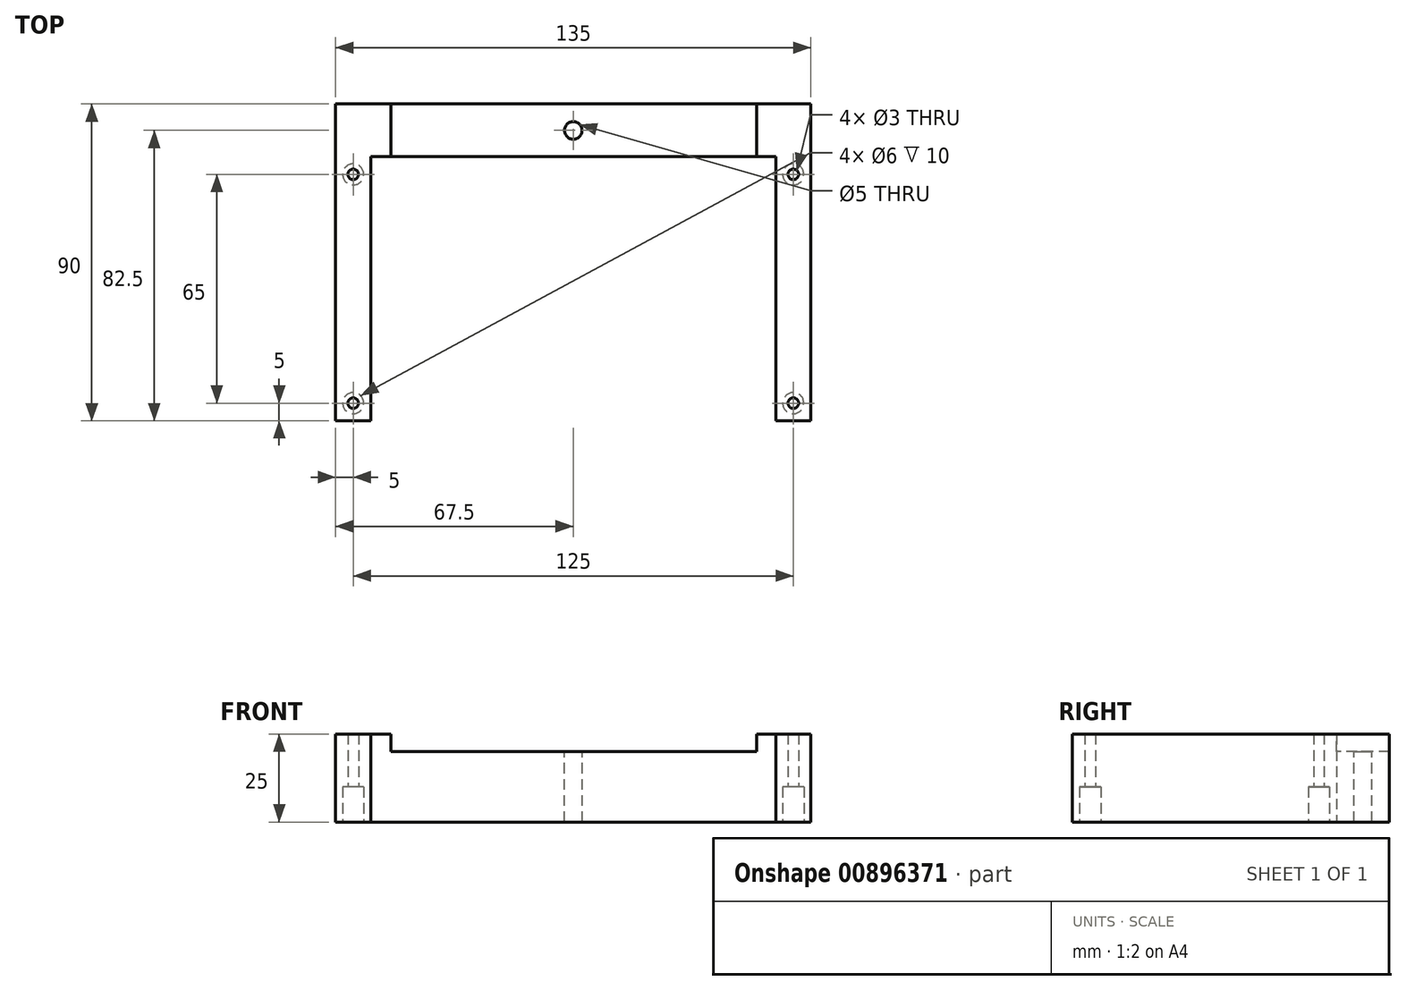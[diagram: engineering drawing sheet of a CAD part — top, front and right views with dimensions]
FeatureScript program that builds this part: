
annotation { "Feature Type Name" : "Feature", "Feature Type Description" : "" }
export const myFeature = defineFeature(function(context is Context, id is Id, definition is map)
    precondition{}
    {
        {
            var Q0;
            Q0=qCreatedBy(makeId("Top.planeOp"),FACE);
            var sketch = newSketch(context, id + "F0", { "sketchPlane" : qUnion([Q0])});
            skCircle(sketch, "E0", {"center": v(-62.5, 65) * mm, "radius": 1.5 * mm});
            skCircle(sketch, "E1", {"center": v(62.5, 65) * mm, "radius": 1.5 * mm});
            skCircle(sketch, "E2", {"center": v(62.5, 0) * mm, "radius": 1.5 * mm});
            skCircle(sketch, "E3", {"center": v(-62.5, 0) * mm, "radius": 1.5 * mm});
            skLineSegment(sketch, "E4", {"start": v(-62.5, 65) * mm, "end": v(62.5, 65) * mm, "construction": true});
            skLineSegment(sketch, "E5", {"start": v(62.5, 0) * mm, "end": v(-62.5, 0) * mm, "construction": true});
            skLineSegment(sketch, "E6", {"start": v(-62.5, 65) * mm, "end": v(-62.5, 0) * mm, "construction": true});
            skLineSegment(sketch, "E7", {"start": v(62.5, 65) * mm, "end": v(62.5, 0) * mm, "construction": true});
            skLineSegment(sketch, "E8.bottom", {"start": v(57.5, 85) * mm, "end": v(67.5, 85) * mm});
            skLineSegment(sketch, "E8.top", {"start": v(57.5, -5) * mm, "end": v(67.5, -5) * mm});
            skLineSegment(sketch, "E8.left", {"start": v(57.5, 85) * mm, "end": v(57.5, -5) * mm});
            skLineSegment(sketch, "E8.right", {"start": v(67.5, 85) * mm, "end": v(67.5, -5) * mm});
            skLineSegment(sketch, "E9.MirrorCS", {"start": v(-57.5, -5) * mm, "end": v(-67.5, -5) * mm});
            skLineSegment(sketch, "E10.MirrorCS", {"start": v(-67.5, 85) * mm, "end": v(-67.5, -5) * mm});
            skLineSegment(sketch, "E11.MirrorCS", {"start": v(-57.5, 85) * mm, "end": v(-57.5, -5) * mm});
            skLineSegment(sketch, "E12.MirrorCS", {"start": v(-57.5, 85) * mm, "end": v(-67.5, 85) * mm});
            skLineSegment(sketch, "E13", {"start": v(62.5, 65) * mm, "end": v(62.5, 80.02) * mm, "construction": true});
            skPoint(sketch, "E14", {"position": v(62.5, 85) * mm});
            skLineSegment(sketch, "E15.bottom", {"start": v(-57.5, 85) * mm, "end": v(57.5, 85) * mm});
            skLineSegment(sketch, "E15.top", {"start": v(-57.5, 70) * mm, "end": v(57.5, 70) * mm});
            skLineSegment(sketch, "E15.left", {"start": v(-57.5, 85) * mm, "end": v(-57.5, 70) * mm});
            skLineSegment(sketch, "E15.right", {"start": v(57.5, 85) * mm, "end": v(57.5, 70) * mm});
            skCircle(sketch, "E16", {"center": v(-62.5, 65) * mm, "radius": 3 * mm});
            skCircle(sketch, "E17", {"center": v(-62.5, 0) * mm, "radius": 3 * mm});
            skCircle(sketch, "E18", {"center": v(62.5, 0) * mm, "radius": 3 * mm});
            skCircle(sketch, "E19", {"center": v(62.5, 65) * mm, "radius": 3 * mm});
            skSolve(sketch);
        }
        {
            var Q0;
            Q0=makeQuery(id+"F0.imprint","IMPRINT",FACE,{"disambiguationData":[TD([[makeQuery(id+"F0.imprint","IMPRINT",EDGE,{"derivedFrom":sQuery(id+"F0.wireOp",EDGE,"E15.bottom")}),-1.0]])]});
            var Q1;
            Q1=makeQuery(id+"F0.imprint","IMPRINT",FACE,{"disambiguationData":[TD([[makeQuery(id+"F0.imprint","IMPRINT",EDGE,{"derivedFrom":sQuery(id+"F0.wireOp",EDGE,"E9.MirrorCS")}),-1.0]])]});
            var Q2;
            Q2=makeQuery(id+"F0.imprint","IMPRINT",FACE,{"disambiguationData":[TD([[makeQuery(id+"F0.imprint","IMPRINT",EDGE,{"derivedFrom":sQuery(id+"F0.wireOp",EDGE,"E8.bottom")}),-1.0]])]});
            var Q3;
            Q3=makeQuery(id+"F0.imprint","IMPRINT",FACE,{"disambiguationData":[TD([[makeQuery(id+"F0.imprint","IMPRINT",EDGE,{"derivedFrom":sQuery(id+"F0.wireOp",EDGE,"E1")}),-1.0]])]});
            var Q4;
            Q4=makeQuery(id+"F0.imprint","IMPRINT",FACE,{"disambiguationData":[TD([[makeQuery(id+"F0.imprint","IMPRINT",EDGE,{"derivedFrom":sQuery(id+"F0.wireOp",EDGE,"E2")}),-1.0]])]});
            var Q5;
            Q5=makeQuery(id+"F0.imprint","IMPRINT",FACE,{"disambiguationData":[TD([[makeQuery(id+"F0.imprint","IMPRINT",EDGE,{"derivedFrom":sQuery(id+"F0.wireOp",EDGE,"E3")}),-1.0]])]});
            var Q6;
            Q6=makeQuery(id+"F0.imprint","IMPRINT",FACE,{"disambiguationData":[TD([[makeQuery(id+"F0.imprint","IMPRINT",EDGE,{"derivedFrom":sQuery(id+"F0.wireOp",EDGE,"E0")}),-1.0]])]});
            extrude(context, id + "F1", {"entities" : qUnion([Q0, Q1, Q2, Q3, Q4, Q5, Q6]), "depth" : 25 * mm, "offsetDistance" : 25 * mm});
        }
        {
            var Q0;
            Q0=makeQuery(id+"F1.opExtrude","CAP_FACE",FACE,{"disambiguationData":[OSD([sQuery(id+"F0.wireOp",EDGE,"E0"),sQuery(id+"F0.wireOp",EDGE,"E1"),sQuery(id+"F0.wireOp",EDGE,"E2"),sQuery(id+"F0.wireOp",EDGE,"E3"),sQuery(id+"F0.wireOp",EDGE,"E8.bottom"),sQuery(id+"F0.wireOp",EDGE,"E8.top"),sQuery(id+"F0.wireOp",EDGE,"E8.left"),sQuery(id+"F0.wireOp",EDGE,"E8.right"),sQuery(id+"F0.wireOp",EDGE,"E9.MirrorCS"),sQuery(id+"F0.wireOp",EDGE,"E10.MirrorCS"),sQuery(id+"F0.wireOp",EDGE,"E11.MirrorCS"),sQuery(id+"F0.wireOp",EDGE,"E12.MirrorCS"),sQuery(id+"F0.wireOp",EDGE,"E15.bottom"),sQuery(id+"F0.wireOp",EDGE,"E15.top")])],"isStart":false});
            var sketch = newSketch(context, id + "F2", { "sketchPlane" : qUnion([Q0])});
            skLineSegment(sketch, "E20", {"start": v(0, 77.5) * mm, "end": v(0, 70) * mm, "construction": true});
            skPoint(sketch, "E20.startSnap0", {"position": v(0, 85) * mm});
            skLineSegment(sketch, "E21", {"start": v(0, 70) * mm, "end": v(0, 85) * mm, "construction": true});
            skCircle(sketch, "E22", {"center": v(0, 77.5) * mm, "radius": 2.5 * mm});
            skLineSegment(sketch, "E23.bottom", {"start": v(-51.79, 85) * mm, "end": v(52.06, 85) * mm});
            skLineSegment(sketch, "E23.top", {"start": v(-51.79, 70) * mm, "end": v(52.06, 70) * mm});
            skLineSegment(sketch, "E23.left", {"start": v(-51.79, 85) * mm, "end": v(-51.79, 70) * mm});
            skLineSegment(sketch, "E23.right", {"start": v(52.06, 85) * mm, "end": v(52.06, 70) * mm});
            skSolve(sketch);
        }
        {
            var Q0;
            Q0=makeQuery(id+"F2.imprint","IMPRINT",FACE,{"disambiguationData":[TD([[makeQuery(id+"F2.imprint","IMPRINT",EDGE,{"derivedFrom":sQuery(id+"F2.wireOp",EDGE,"E22")}),1.0]])]});
            extrude(context, id + "F3", {"entities" : qUnion([Q0]), "operationType" : NewBodyOperationType.REMOVE, "oppositeDirection" : true, "depth" : 25 * mm, "offsetDistance" : 25 * mm});
        }
        {
            var Q0;
            Q0=makeQuery(id+"F2.imprint","IMPRINT",FACE,{"disambiguationData":[TD([[makeQuery(id+"F2.imprint","IMPRINT",EDGE,{"derivedFrom":sQuery(id+"F2.wireOp",EDGE,"E22")}),-1.0]])]});
            extrude(context, id + "F4", {"entities" : qUnion([Q0]), "operationType" : NewBodyOperationType.REMOVE, "oppositeDirection" : true, "depth" : 5 * mm, "offsetDistance" : 25 * mm});
        }
        {
            var Q0;
            Q0=makeQuery(id+"F0.imprint","IMPRINT",FACE,{"disambiguationData":[TD([[makeQuery(id+"F0.imprint","IMPRINT",EDGE,{"derivedFrom":sQuery(id+"F0.wireOp",EDGE,"E0")}),-1.0]])]});
            var Q1;
            Q1=makeQuery(id+"F0.imprint","IMPRINT",FACE,{"disambiguationData":[TD([[makeQuery(id+"F0.imprint","IMPRINT",EDGE,{"derivedFrom":sQuery(id+"F0.wireOp",EDGE,"E3")}),-1.0]])]});
            var Q2;
            Q2=makeQuery(id+"F0.imprint","IMPRINT",FACE,{"disambiguationData":[TD([[makeQuery(id+"F0.imprint","IMPRINT",EDGE,{"derivedFrom":sQuery(id+"F0.wireOp",EDGE,"E2")}),-1.0]])]});
            var Q3;
            Q3=makeQuery(id+"F0.imprint","IMPRINT",FACE,{"disambiguationData":[TD([[makeQuery(id+"F0.imprint","IMPRINT",EDGE,{"derivedFrom":sQuery(id+"F0.wireOp",EDGE,"E1")}),-1.0]])]});
            extrude(context, id + "F5", {"entities" : qUnion([Q0, Q1, Q2, Q3]), "operationType" : NewBodyOperationType.REMOVE, "depth" : 10 * mm, "offsetDistance" : 25 * mm});
        }
    });
